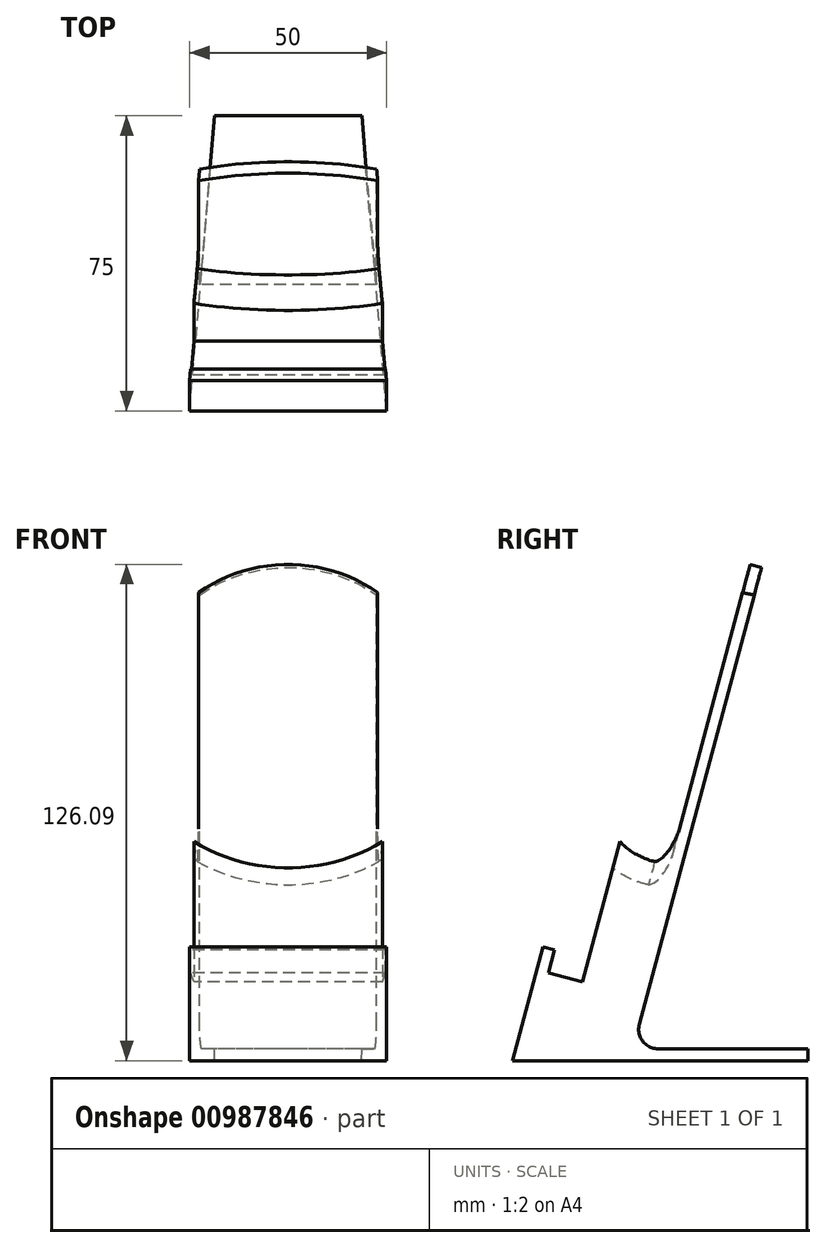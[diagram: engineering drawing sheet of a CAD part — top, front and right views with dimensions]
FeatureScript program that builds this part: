
annotation { "Feature Type Name" : "Feature", "Feature Type Description" : "" }
export const myFeature = defineFeature(function(context is Context, id is Id, definition is map)
    precondition{}
    {
        {
            var Q0;
            Q0=qCreatedBy(makeId("Right.planeOp"),FACE);
            var sketch = newSketch(context, id + "F0", { "sketchPlane" : qUnion([Q0])});
            skLineSegment(sketch, "E0", {"start": v(38.45, 0) * mm, "end": v(-36.55, 0) * mm});
            skLineSegment(sketch, "E1", {"start": v(-36.55, 0) * mm, "end": v(-28.8, 28.9) * mm});
            skLineSegment(sketch, "E2", {"start": v(-28.8, 28.9) * mm, "end": v(-25.9, 28.12) * mm});
            skLineSegment(sketch, "E3", {"start": v(-25.9, 28.12) * mm, "end": v(-27.46, 22.33) * mm});
            skLineSegment(sketch, "E4", {"start": v(-27.46, 22.33) * mm, "end": v(-18.77, 20) * mm});
            skLineSegment(sketch, "E5", {"start": v(-18.77, 20) * mm, "end": v(12.68, 137.36) * mm});
            skLineSegment(sketch, "E6", {"start": v(12.68, 137.36) * mm, "end": v(28.8, 133.04) * mm});
            skLineSegment(sketch, "E7", {"start": v(28.8, 133.04) * mm, "end": v(-4.35, 9.3) * mm});
            skLineSegment(sketch, "E8", {"start": v(0.48, 3) * mm, "end": v(38.45, 3) * mm});
            skLineSegment(sketch, "E9", {"start": v(38.45, 3) * mm, "end": v(38.45, 0) * mm});
            skPoint(sketch, "E10", {"position": v(0.64, 92.44) * mm});
            skPoint(sketch, "E11.visualSharp", {"position": v(-6.03, 3) * mm});
            skArc(sketch, "E11.filletArc", {"start": v(-4.35, 9.3) * mm, "mid": v(-3.49, 4.96) * mm, "end": v(0.48, 3) * mm});
            skSolve(sketch);
        }
        {
            var Q0;
            Q0 = qSketchRegion(id + "F0", true);
            extrude(context, id + "F1", {"entities" : qUnion([Q0]), "endBound" : BoundingType.SYMMETRIC, "depth" : 50 * mm, "offsetDistance" : 25 * mm});
        }
        {
            var Q0;
            Q0=qCreatedBy(makeId("Right.planeOp"),FACE);
            var sketch = newSketch(context, id + "F2", { "sketchPlane" : qUnion([Q0])});
            skLineSegment(sketch, "E12.0", {"start": v(-18.77, 20) * mm, "end": v(12.68, 137.36) * mm, "construction": true});
            skPoint(sketch, "E13", {"position": v(0.64, 92.44) * mm});
            skLineSegment(sketch, "E14", {"start": v(0.64, 92.44) * mm, "end": v(12.29, 135.91) * mm});
            skFitSpline(sketch, "E15", {"points": [v(12.29, 135.91) * mm, v(22.22, 135.11) * mm], "startDerivative": vector(11.2, 2.42) * mm, "endDerivative": vector(5.55, -2.07) * mm});
            skFitSpline(sketch, "E16", {"points": [v(22.22, 135.11) * mm, v(23.84, 126.09) * mm], "startDerivative": vector(6.5, -4.54) * mm, "endDerivative": vector(-1.6, -5.91) * mm});
            skLineSegment(sketch, "E17", {"start": v(23.84, 126.09) * mm, "end": v(13.88, 88.9) * mm});
            skLineSegment(sketch, "E18", {"start": v(13.88, 88.9) * mm, "end": v(0.64, 92.44) * mm});
            skLineSegment(sketch, "E19", {"start": v(22.22, 135.11) * mm, "end": v(10.1, 89.9) * mm, "construction": true});
            skSolve(sketch);
        }
        {
            var Q0;
            Q0 = qSketchRegion(id + "F2", true);
            var Q1;
            Q1=sQuery(id+"F2.wireOp",EDGE,"E18");
            revolve(context, id + "F3", {"operationType" : NewBodyOperationType.REMOVE, "surfaceOperationType" : NewSurfaceOperationType.NEW, "entities" : qUnion([Q0]), "axis" : qUnion([Q1]), "revolveType" : RevolveType.FULL, "oppositeDirection" : true});
        }
        {
            var Q0;
            Q0=makeQuery(id+"F1.opExtrude","SWEPT_FACE",FACE,{"disambiguationData":[OSD([sQuery(id+"F0.wireOp",EDGE,"E7")])]});
            var sketch = newSketch(context, id + "F4", { "sketchPlane" : qUnion([Q0])});
            skLineSegment(sketch, "E20.0.0", {"start": v(25, 7.85) * mm, "end": v(25, 135.96) * mm});
            skLineSegment(sketch, "E20.0.1", {"start": v(25, 135.96) * mm, "end": v(-25, 135.96) * mm});
            skLineSegment(sketch, "E20.0.2", {"start": v(-25, 135.96) * mm, "end": v(-25, 7.85) * mm});
            skLineSegment(sketch, "E20.0.3", {"start": v(-25, 7.85) * mm, "end": v(25, 7.85) * mm});
            skArc(sketch, "E21.0", {"start": v(-25, 118.74) * mm, "mid": v(0, 127.96) * mm, "end": v(25, 118.74) * mm});
            skSolve(sketch);
        }
        {
            var Q0;
            {var subQ0=sQuery(id+"F4.wireOp",EDGE,"E20.0.1");Q0=makeQuery(id+"F4.imprint","IMPRINT",FACE,{"disambiguationData":[TD([[makeQuery(id+"F4.imprint","IMPRINT",EDGE,{"derivedFrom":subQ0}),-1.0]])]});}
            var Q1;
            {var subQ4=sQuery(id+"F0.wireOp",EDGE,"E6");var subQ5=sQuery(id+"F0.wireOp",EDGE,"E5");Q1=makeQuery(id+"F3.boolean.opBoolean","SPLIT",FACE,{"disambiguationData":[TD([makeQuery(id+"F1.opExtrude","SWEPT_FACE",FACE,{"disambiguationData":[OSD([subQ4])]})])],"derivedFrom":makeQuery(id+"F1.opExtrude","SWEPT_FACE",FACE,{"disambiguationData":[OSD([subQ5])]})});}
            extrude(context, id + "F5", {"entities" : qUnion([Q0]), "operationType" : NewBodyOperationType.REMOVE, "endBound" : BoundingType.UP_TO_SURFACE, "oppositeDirection" : true, "depth" : 30 * mm, "endBoundEntityFace" : qUnion([Q1]), "offsetDistance" : 25 * mm});
        }
        {
            var Q0;
            Q0=makeQuery(id+"F1.opExtrude","SWEPT_FACE",FACE,{"disambiguationData":[OSD([sQuery(id+"F0.wireOp",EDGE,"E0")])]});
            var Q1;
            Q1=makeQuery(id+"F1.opExtrude","SWEPT_EDGE",EDGE,{"disambiguationData":[OSD([sQuery(id+"F0.wireOp",EDGE,"E0"),sQuery(id+"F0.wireOp",EDGE,"E1")])]});
            cPlane(context, id + "F6", {"entities" : qUnion([Q0, Q1]), "cplaneType" : CPlaneType.LINE_ANGLE, "offset" : 25 * mm, "angle" : 15 * degree, "width" : 150 * mm, "height" : 150 * mm});
        }
        {
            var Q0;
            Q0=qCreatedBy(id+"F6.planeOp",FACE);
            var sketch = newSketch(context, id + "F7", { "sketchPlane" : qUnion([Q0])});
            skLineSegment(sketch, "E22.0.0", {"start": v(-25, -35.3) * mm, "end": v(-25, 37.14) * mm});
            skLineSegment(sketch, "E22.0.1", {"start": v(-25, 37.14) * mm, "end": v(25, 37.14) * mm});
            skLineSegment(sketch, "E22.0.2", {"start": v(25, 37.14) * mm, "end": v(25, -35.3) * mm});
            skLineSegment(sketch, "E22.0.3", {"start": v(25, -35.3) * mm, "end": v(-25, -35.3) * mm});
            skLineSegment(sketch, "E23", {"start": v(-25, -35.3) * mm, "end": v(-18.66, 37.14) * mm});
            skLineSegment(sketch, "E24", {"start": v(25, -35.3) * mm, "end": v(18.66, 37.14) * mm});
            skSolve(sketch);
        }
        {
            var Q0;
            {var subQ0=sQuery(id+"F7.wireOp",EDGE,"E22.0.0");Q0=makeQuery(id+"F7.imprint","IMPRINT",FACE,{"disambiguationData":[TD([[makeQuery(id+"F7.imprint","IMPRINT",EDGE,{"derivedFrom":subQ0}),-1.0]])]});}
            var Q1;
            {var subQ0=sQuery(id+"F7.wireOp",EDGE,"E22.0.2");Q1=makeQuery(id+"F7.imprint","IMPRINT",FACE,{"disambiguationData":[TD([[makeQuery(id+"F7.imprint","IMPRINT",EDGE,{"derivedFrom":subQ0}),-1.0]])]});}
            extrude(context, id + "F8", {"entities" : qUnion([Q0, Q1]), "operationType" : NewBodyOperationType.REMOVE, "endBound" : BoundingType.THROUGH_ALL, "depth" : 25 * mm, "offsetDistance" : 25 * mm});
        }
    });
